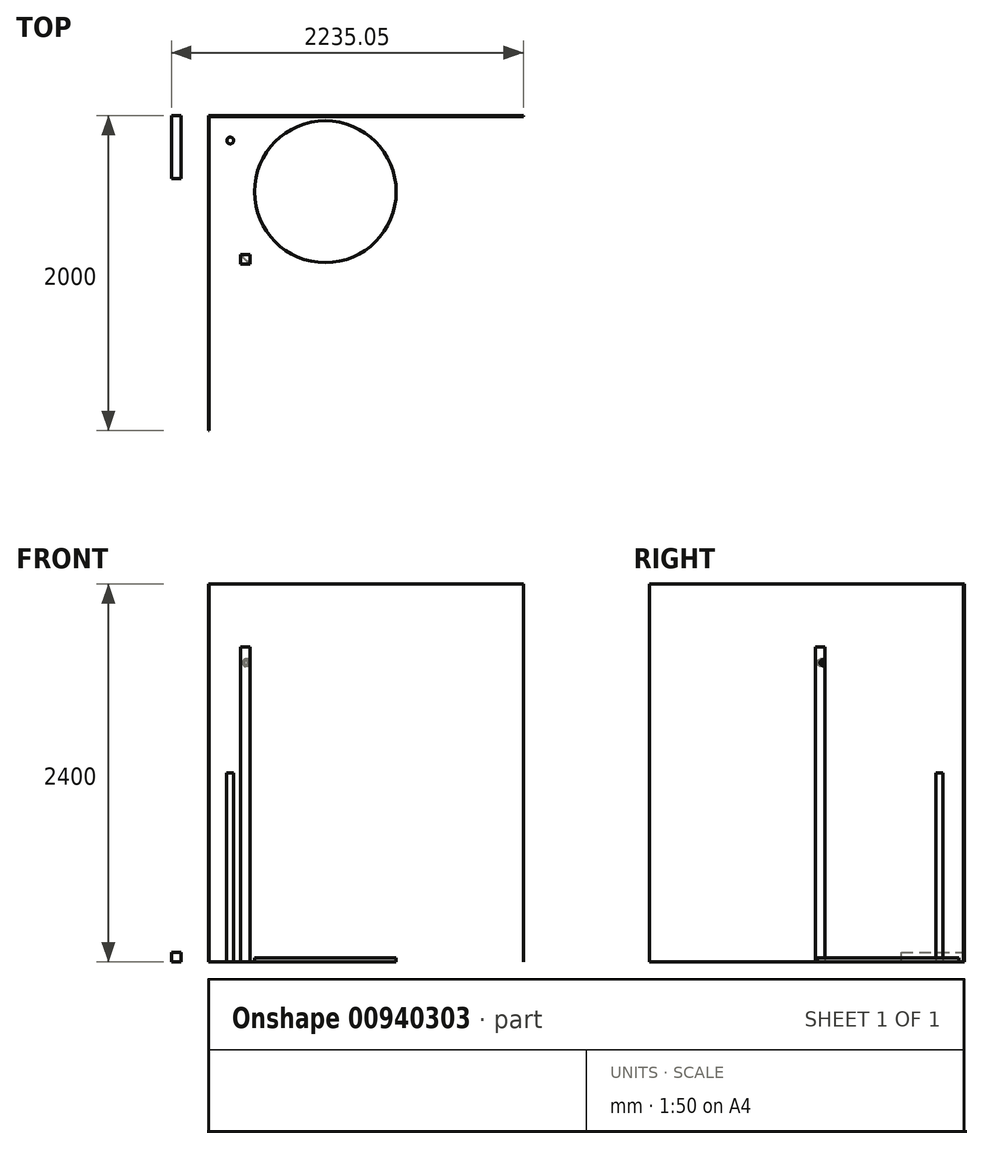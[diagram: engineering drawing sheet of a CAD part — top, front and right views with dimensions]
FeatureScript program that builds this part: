
annotation { "Feature Type Name" : "Feature", "Feature Type Description" : "" }
export const myFeature = defineFeature(function(context is Context, id is Id, definition is map)
    precondition{}
    {
        {
            var Q0;
            Q0=qCreatedBy(makeId("Top.planeOp"),FACE);
            var sketch = newSketch(context, id + "F0", { "sketchPlane" : qUnion([Q0])});
            skLineSegment(sketch, "E0", {"start": v(2000, 0) * mm, "end": v(0, 0) * mm});
            skLineSegment(sketch, "E1", {"start": v(0, 0) * mm, "end": v(0, -2000) * mm});
            skSolve(sketch);
        }
        {
            var Q0;
            Q0=sQuery(id+"F0.wireOp",EDGE,"E0");
            var Q1;
            Q1=sQuery(id+"F0.wireOp",EDGE,"E1");
            extrude(context, id + "F1", {"bodyType" : ToolBodyType.SURFACE, "surfaceEntities" : qUnion([Q0, Q1]), "depth" : 2400 * mm, "offsetDistance" : 25 * mm});
        }
        {
            var Q0;
            Q0=qCreatedBy(makeId("Top.planeOp"),FACE);
            var sketch = newSketch(context, id + "F2", { "sketchPlane" : qUnion([Q0])});
            skLineSegment(sketch, "E2.bottom", {"start": v(203.34, -883.75) * mm, "end": v(263.34, -883.75) * mm});
            skLineSegment(sketch, "E2.top", {"start": v(203.34, -943.75) * mm, "end": v(263.34, -943.75) * mm});
            skLineSegment(sketch, "E2.left", {"start": v(203.34, -883.75) * mm, "end": v(203.34, -943.75) * mm});
            skLineSegment(sketch, "E2.right", {"start": v(263.34, -883.75) * mm, "end": v(263.34, -943.75) * mm});
            skSolve(sketch);
        }
        {
            var Q0;
            Q0=makeQuery(id+"F2.imprint","IMPRINT",FACE,{"disambiguationData":[TD([[makeQuery(id+"F2.imprint","IMPRINT",EDGE,{"derivedFrom":sQuery(id+"F2.wireOp",EDGE,"E2.bottom")}),-1.0]])]});
            extrude(context, id + "F3", {"entities" : qUnion([Q0]), "depth" : 2000 * mm, "offsetDistance" : 25 * mm});
        }
        {
            var Q0;
            Q0=makeQuery(id+"F1.opExtrude","SWEPT_FACE",FACE,{"disambiguationData":[OSD([sQuery(id+"F0.wireOp",EDGE,"E1")])]});
            extrude(context, id + "F4", {"entities" : qUnion([Q0]), "oppositeDirection" : true, "depth" : 5 * mm, "offsetDistance" : 25 * mm});
        }
        {
            var Q0;
            Q0=makeQuery(id+"F1.opExtrude","SWEPT_FACE",FACE,{"disambiguationData":[OSD([sQuery(id+"F0.wireOp",EDGE,"E0")])]});
            extrude(context, id + "F5", {"entities" : qUnion([Q0]), "operationType" : NewBodyOperationType.ADD, "oppositeDirection" : true, "depth" : 5 * mm, "offsetDistance" : 25 * mm});
        }
        {
            var Q0;
            Q0=qCreatedBy(makeId("Top.planeOp"),FACE);
            var sketch = newSketch(context, id + "F6", { "sketchPlane" : qUnion([Q0])});
            skCircle(sketch, "E3", {"center": v(138.33, -157.97) * mm, "radius": 21.5 * mm});
            skSolve(sketch);
        }
        {
            var Q0;
            Q0=makeQuery(id+"F6.imprint","IMPRINT",FACE,{"disambiguationData":[TD([[makeQuery(id+"F6.imprint","IMPRINT",EDGE,{"derivedFrom":sQuery(id+"F6.wireOp",EDGE,"E3")}),1.0]])]});
            extrude(context, id + "F7", {"entities" : qUnion([Q0]), "depth" : 1200 * mm, "offsetDistance" : 25 * mm});
        }
        {
            var Q0;
            Q0=makeQuery(id+"F3.opExtrude","SWEPT_EDGE",EDGE,{"disambiguationData":[OSD([sQuery(id+"F2.wireOp",EDGE,"E2.bottom"),sQuery(id+"F2.wireOp",EDGE,"E2.left")])]});
            var Q1;
            Q1=makeQuery(id+"F3.opExtrude","SWEPT_EDGE",EDGE,{"disambiguationData":[OSD([sQuery(id+"F2.wireOp",EDGE,"E2.top"),sQuery(id+"F2.wireOp",EDGE,"E2.right")])]});
            cPlane(context, id + "F8", {"entities" : qUnion([Q0, Q1]), "cplaneType" : CPlaneType.LINE_ANGLE, "offset" : 25 * mm, "angle" : 0 * degree, "width" : 150 * mm, "height" : 150 * mm});
        }
        {
            var Q0;
            Q0=qCreatedBy(id+"F8.planeOp",FACE);
            var sketch = newSketch(context, id + "F9", { "sketchPlane" : qUnion([Q0])});
            skLineSegment(sketch, "E4.0", {"start": v(811.11, 2000) * mm, "end": v(811.11, 0) * mm});
            skCircle(sketch, "E5", {"center": v(811.11, 1900) * mm, "radius": 22.5 * mm});
            skSolve(sketch);
        }
        {
            var Q0;
            {var subQ0=sQuery(id+"F9.wireOp",EDGE,"E5");var subQ1=sQuery(id+"F9.wireOp",EDGE,"E4.0");var subQ2=makeQuery(id+"F9.imprint","INTERSECT",VERTEX,{"disambiguationData":[OD(0.0)],"derivedFrom":[subQ1,subQ0]});Q0=makeQuery(id+"F9.imprint","IMPRINT",FACE,{"disambiguationData":[TD([[makeQuery(id+"F9.imprint","IMPRINT",EDGE,{"disambiguationData":[TD([[subQ2,1.0]])],"derivedFrom":subQ1}),1.0]])]});}
            var Q1;
            {var subQ0=sQuery(id+"F9.wireOp",EDGE,"E5");var subQ1=sQuery(id+"F9.wireOp",EDGE,"E4.0");var subQ2=makeQuery(id+"F9.imprint","INTERSECT",VERTEX,{"disambiguationData":[OD(0.0)],"derivedFrom":[subQ1,subQ0]});Q1=makeQuery(id+"F9.imprint","IMPRINT",FACE,{"disambiguationData":[TD([[makeQuery(id+"F9.imprint","IMPRINT",EDGE,{"disambiguationData":[TD([[subQ2,1.0]])],"derivedFrom":subQ1}),-1.0]])]});}
            extrude(context, id + "F10", {"entities" : qUnion([Q0, Q1]), "operationType" : NewBodyOperationType.REMOVE, "oppositeDirection" : true, "depth" : 76 * mm, "offsetDistance" : 25 * mm});
        }
        {
            var Q0;
            Q0=makeQuery(id+"F3.opExtrude","CAP_FACE",FACE,{"disambiguationData":[OSD([sQuery(id+"F2.wireOp",EDGE,"E2.bottom"),sQuery(id+"F2.wireOp",EDGE,"E2.top"),sQuery(id+"F2.wireOp",EDGE,"E2.left"),sQuery(id+"F2.wireOp",EDGE,"E2.right")])],"isStart":false});
            cPlane(context, id + "F11", {"entities" : qUnion([Q0]), "cplaneType" : CPlaneType.OFFSET, "offset" : 1025 * mm, "oppositeDirection" : true, "width" : 150 * mm, "height" : 150 * mm});
        }
        {
            var Q0;
            Q0=qCreatedBy(makeId("Top.planeOp"),FACE);
            var sketch = newSketch(context, id + "F12", { "sketchPlane" : qUnion([Q0])});
            skCircle(sketch, "E6", {"center": v(742.59, -483) * mm, "radius": 450 * mm});
            skSolve(sketch);
        }
        {
            var Q0;
            Q0=makeQuery(id+"F12.imprint","IMPRINT",FACE,{"disambiguationData":[TD([[makeQuery(id+"F12.imprint","IMPRINT",EDGE,{"derivedFrom":sQuery(id+"F12.wireOp",EDGE,"E6")}),1.0]])]});
            extrude(context, id + "F13", {"entities" : qUnion([Q0]), "depth" : 25 * mm, "offsetDistance" : 25 * mm});
        }
        {
            var Q0;
            Q0=qCreatedBy(makeId("Front.planeOp"),FACE);
            var sketch = newSketch(context, id + "F14", { "sketchPlane" : qUnion([Q0])});
            skLineSegment(sketch, "E7.bottom", {"start": v(-175.05, 0) * mm, "end": v(-235.05, 0) * mm});
            skLineSegment(sketch, "E7.top", {"start": v(-175.05, 60) * mm, "end": v(-235.05, 60) * mm});
            skLineSegment(sketch, "E7.left", {"start": v(-175.05, 0) * mm, "end": v(-175.05, 60) * mm});
            skLineSegment(sketch, "E7.right", {"start": v(-235.05, 0) * mm, "end": v(-235.05, 60) * mm});
            skSolve(sketch);
        }
        {
            var Q0;
            Q0=makeQuery(id+"F14.imprint","IMPRINT",FACE,{"disambiguationData":[TD([[makeQuery(id+"F14.imprint","IMPRINT",EDGE,{"derivedFrom":sQuery(id+"F14.wireOp",EDGE,"E7.bottom")}),-1.0]])]});
            extrude(context, id + "F15", {"entities" : qUnion([Q0]), "depth" : 400 * mm, "offsetDistance" : 25 * mm});
        }
    });
